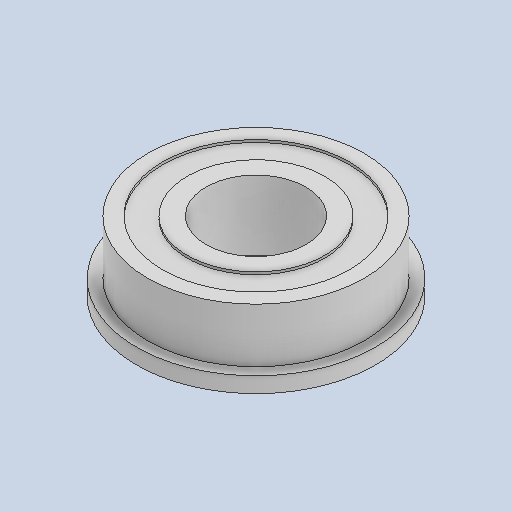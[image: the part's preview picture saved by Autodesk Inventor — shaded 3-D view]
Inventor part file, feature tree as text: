
AUTODESK INVENTOR PART (.ipt)
format: ipt  version: 2022.3 (Build 263350000, 350)  size: 135,168 bytes
history: native  units: in
note: dims shown in document units (in); Inventor stores cm internally (conversion verified against a paired STEP export)
features: revolve x1
ambient origin geometry x8: Origin, YZ Plane, XZ Plane, XY Plane, X Axis, Y Axis, Z Axis, Center Point
bodies: Solid1 (feature_tree)
feature tree (1):
  revolve  "Revolve1"  [1 undecoded]
note: 1 required parameter value undecoded (feature->parameter linkage not recoverable at this tier; creation-order binding heuristic only, values carry confidence <= 0.55)
